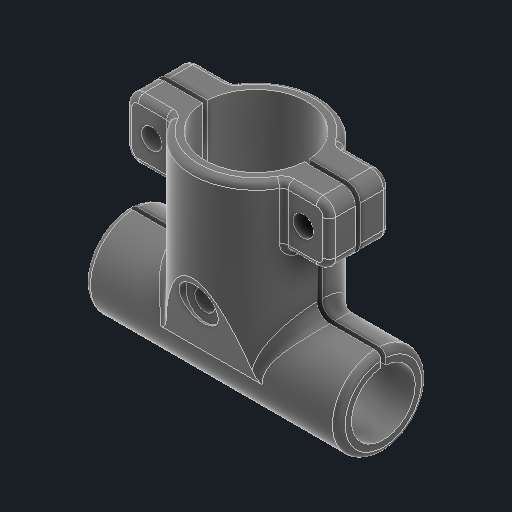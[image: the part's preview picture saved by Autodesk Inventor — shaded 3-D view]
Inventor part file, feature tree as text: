
AUTODESK INVENTOR PART (.ipt)
format: ipt  version: 2025 (Build 290162010, 162A)  size: 550,912 bytes
history: native  units: mm
features: sketch x11, extrude x10, projected_geometry x7, fillet x4, revolve x2, plane x2
ambient origin geometry x8: Origin, YZ Plane, XZ Plane, XY Plane, X Axis, Y Axis, Z Axis, Center Point
bodies: Solid1 (feature_tree)
feature tree (36):
  sketch  "Sketch1"  dims[d0=40.0mm d1=20.0mm]
  revolve  "Revolution1"  [1 undecoded]
  revolve  "Revolution2"  [1 undecoded]
  extrude  "Extrusion1"  Depth=2.0mm
  extrude  "Extrusion2"  Depth=4.0mm
  extrude  "Extrusion3"  TaperAngle=360.0deg  [1 undecoded]
  extrude  "Extrusion4"  Depth=15.0mm
  extrude  "Extrusion5"  Depth=4.5mm
  plane  "Work Plane1"
  plane  "Work Plane2"
  extrude  "Extrusion6"  Depth=9.5mm
  extrude  "Extrusion7"  Depth=9.5mm
  fillet  "Fillet1"  Radius=9.5mm
  fillet  "Fillet2"  Radius=4.1mm
  fillet  "Fillet3"  Radius=4.1mm
  fillet  "Fillet4"  Radius=3.2mm
  extrude  "Extrusion8"  Depth=9.5mm TaperAngle=0.0deg
  extrude  "Extrusion9"  Depth=10.0mm
  extrude  "Extrusion11"  Depth=10.0mm TaperAngle=0.0deg
  sketch  "Sketch2"  dims[d2=27.0mm d3=6.0mm]
  projected_geometry  "Projected Loop1"
  projected_geometry  "Projected Loop2"
  sketch  "Sketch3"  dims[d4=40.0mm d5=2.0mm]
  sketch  "Sketch4"  dims[d7=8.0mm d8=4.0mm]
  projected_geometry  "Projected Loop3"
  projected_geometry  "Projected Loop4"
  sketch  "Sketch5"  dims[d9=27.0mm d10=360.0deg]
  projected_geometry  "Projected Loop5"
  projected_geometry  "Projected Loop6"
  sketch  "Sketch6"  dims[d11=90.0deg d12=15.0mm]
  projected_geometry  "Projected Loop7"
  sketch  "Sketch7"  dims[d13=23.0mm d14=0.0mm d15=4.5mm]
  sketch  "Sketch8"  dims[d16=16.0mm d17=9.5mm]
  sketch  "Sketch9"  dims[d18=32.0mm d19=9.5mm d20=9.5mm d21=0.0mm d22=4.1mm d23=4.1mm d24=3.2mm]
  sketch  "Sketch10"  dims[d25=3.2mm d26=9.5mm d27=0.0mm]
  sketch  "Sketch12"  dims[d28=3.2mm d29=3.2mm d30=2.0mm d31=0.0mm d32=8.0mm d33=3.2mm d34=0.0mm d35=0.0mm d36=10.0mm d37=-10.0mm d38=6.0mm d39=2.0mm d40=0.0mm d42=2.0mm d43=0.0mm d44=2.0mm d45=2.0mm d46=1.0mm d47=1.0mm d48=27.0mm d49=0.75mm d50=27.0mm d51=10.0mm d52=0.0mm d53=0.0mm d54=3.2mm d55=16.0mm d56=15.0mm d57=0.0mm d61=6.0mm d62=12.25mm d63=0.0mm]
note: 3 required parameter values undecoded (feature->parameter linkage not recoverable at this tier; creation-order binding heuristic only, values carry confidence <= 0.55)